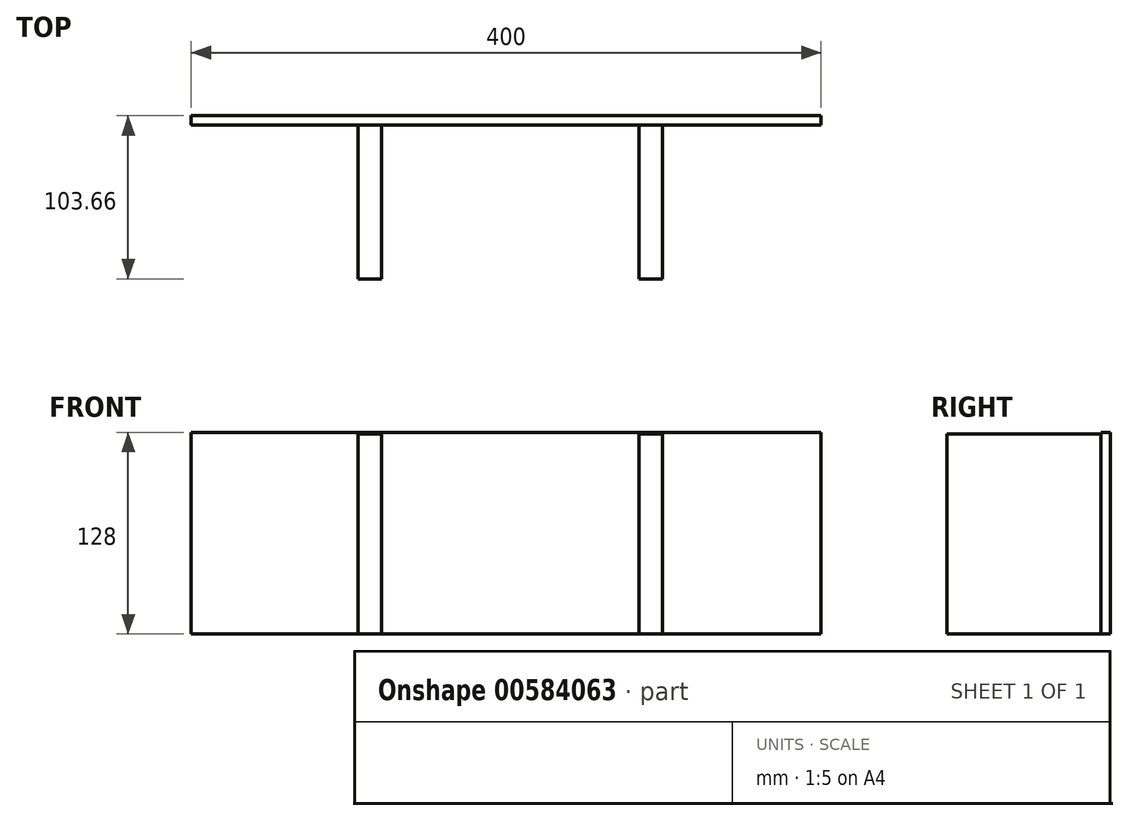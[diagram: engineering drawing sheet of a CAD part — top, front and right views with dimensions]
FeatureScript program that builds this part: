
annotation { "Feature Type Name" : "Feature", "Feature Type Description" : "" }
export const myFeature = defineFeature(function(context is Context, id is Id, definition is map)
    precondition{}
    {
        {
            var Q0;
            Q0=qCreatedBy(makeId("Top.planeOp"),FACE);
            var sketch = newSketch(context, id + "F0", { "sketchPlane" : qUnion([Q0])});
            skLineSegment(sketch, "E0", {"start": v(0, 0) * mm, "end": v(-400, 0) * mm});
            skLineSegment(sketch, "E1", {"start": v(-400, 0) * mm, "end": v(-400, 6) * mm});
            skLineSegment(sketch, "E2", {"start": v(-400, 6) * mm, "end": v(0, 6) * mm});
            skLineSegment(sketch, "E3", {"start": v(-288.1, 0) * mm, "end": v(-288.1, 135.12) * mm});
            skLineSegment(sketch, "E4", {"start": v(-107.92, 135.12) * mm, "end": v(-107.92, 0) * mm});
            skFitSpline(sketch, "E5", {"points": [v(-288.1, 135.12) * mm, v(-400, 6) * mm], "startDerivative": vector(-80.86, -186.65) * mm, "endDerivative": vector(-112.78, -106.22) * mm});
            skFitSpline(sketch, "E6", {"points": [v(-288.1, 135.12) * mm, v(-227.53, 52.45) * mm, v(-188.43, 41.47) * mm, v(-107.92, 135.12) * mm], "startDerivative": vector(134.06, -172.38) * mm, "endDerivative": vector(416.65, 700.38) * mm});
            skFitSpline(sketch, "E7", {"points": [v(-107.92, 135.12) * mm, v(-83.39, 92.79) * mm, v(0, 6) * mm], "startDerivative": vector(-18.81, 13.3) * mm, "endDerivative": vector(158.87, -141.96) * mm});
            skLineSegment(sketch, "E8", {"start": v(-376.94, 26.68) * mm, "end": v(-376.94, 6) * mm});
            skLineSegment(sketch, "E9", {"start": v(-362.4, 41.4) * mm, "end": v(-362.4, 6) * mm});
            skLineSegment(sketch, "E10", {"start": v(-348.72, 52.04) * mm, "end": v(-348.72, 6) * mm});
            skLineSegment(sketch, "E11", {"start": v(-335.96, 64.72) * mm, "end": v(-335.96, 6) * mm});
            skLineSegment(sketch, "E12", {"start": v(-322.75, 79.43) * mm, "end": v(-322.75, 6) * mm});
            skLineSegment(sketch, "E13", {"start": v(-311.95, 93.3) * mm, "end": v(-311.95, 6) * mm});
            skLineSegment(sketch, "E14", {"start": v(-299.65, 112.23) * mm, "end": v(-299.65, 6) * mm});
            skLineSegment(sketch, "E15", {"start": v(-272.67, 112.23) * mm, "end": v(-272.67, 6) * mm});
            skLineSegment(sketch, "E16", {"start": v(-260.72, 93.3) * mm, "end": v(-260.72, 6) * mm});
            skLineSegment(sketch, "E17", {"start": v(-240.1, 64.72) * mm, "end": v(-240.1, 6) * mm});
            skLineSegment(sketch, "E18", {"start": v(-251.42, 79.43) * mm, "end": v(-251.42, 6) * mm});
            skLineSegment(sketch, "E19", {"start": v(-227.53, 52.45) * mm, "end": v(-227.53, 6) * mm});
            skLineSegment(sketch, "E20", {"start": v(-216.13, 45.83) * mm, "end": v(-216.13, 6) * mm});
            skLineSegment(sketch, "E21", {"start": v(-205.23, 42.66) * mm, "end": v(-205.23, 6) * mm});
            skLineSegment(sketch, "E22", {"start": v(-188.43, 41.47) * mm, "end": v(-188.43, 6) * mm});
            skLineSegment(sketch, "E23", {"start": v(-175.91, 42.85) * mm, "end": v(-175.91, 6) * mm});
            skLineSegment(sketch, "E24", {"start": v(-164.84, 50.37) * mm, "end": v(-164.84, 6) * mm});
            skLineSegment(sketch, "E25", {"start": v(-152.72, 64.72) * mm, "end": v(-152.72, 6) * mm});
            skLineSegment(sketch, "E26", {"start": v(-142.44, 79.43) * mm, "end": v(-142.44, 6) * mm});
            skLineSegment(sketch, "E27", {"start": v(-130.69, 97.68) * mm, "end": v(-130.69, 6) * mm});
            skLineSegment(sketch, "E28", {"start": v(-120.01, 115) * mm, "end": v(-120.01, 6) * mm});
            skLineSegment(sketch, "E29", {"start": v(-97.77, 115) * mm, "end": v(-97.77, 6) * mm});
            skLineSegment(sketch, "E30", {"start": v(-83.39, 97.68) * mm, "end": v(-83.39, 6) * mm});
            skLineSegment(sketch, "E31", {"start": v(-73.37, 79.43) * mm, "end": v(-73.37, 6) * mm});
            skLineSegment(sketch, "E32", {"start": v(-60.95, 64.72) * mm, "end": v(-60.95, 6) * mm});
            skLineSegment(sketch, "E33", {"start": v(-47.5, 50.37) * mm, "end": v(-47.5, 6) * mm});
            skLineSegment(sketch, "E34", {"start": v(-32.34, 34.9) * mm, "end": v(-32.34, 6) * mm});
            skLineSegment(sketch, "E35", {"start": v(-21.72, 25.6) * mm, "end": v(-21.72, 6) * mm});
            skLineSegment(sketch, "E36", {"start": v(-288.1, 135.12) * mm, "end": v(-288.1, -8.35) * mm});
            skLineSegment(sketch, "E37", {"start": v(-294.13, 122.34) * mm, "end": v(-294.13, -97.66) * mm});
            skLineSegment(sketch, "E38", {"start": v(-279.13, 122.34) * mm, "end": v(-279.13, -97.66) * mm});
            skLineSegment(sketch, "E39", {"start": v(-294.13, -97.66) * mm, "end": v(-279.13, -97.66) * mm});
            skLineSegment(sketch, "E40", {"start": v(-115.57, 122.34) * mm, "end": v(-115.57, -97.66) * mm});
            skLineSegment(sketch, "E41", {"start": v(-115.57, -97.66) * mm, "end": v(-100.57, -97.66) * mm});
            skLineSegment(sketch, "E42", {"start": v(-100.57, -97.66) * mm, "end": v(-100.57, 122.34) * mm});
            skLineSegment(sketch, "E43", {"start": v(0, 6) * mm, "end": v(0, 0) * mm});
            skSolve(sketch);
        }
        {
            var Q0;
            Q0=sQuery(id+"F0.wireOp",EDGE,"E8");
            var Q1;
            Q1=sQuery(id+"F0.wireOp",EDGE,"E9");
            var Q2;
            Q2=sQuery(id+"F0.wireOp",EDGE,"E10");
            var Q3;
            Q3=sQuery(id+"F0.wireOp",EDGE,"E11");
            var Q4;
            Q4=sQuery(id+"F0.wireOp",EDGE,"E12");
            var Q5;
            Q5=sQuery(id+"F0.wireOp",EDGE,"E13");
            var Q6;
            Q6=sQuery(id+"F0.wireOp",EDGE,"E14");
            var Q7;
            Q7=sQuery(id+"F0.wireOp",EDGE,"E37");
            var Q8;
            Q8=sQuery(id+"F0.wireOp",EDGE,"E38");
            var Q9;
            Q9=sQuery(id+"F0.wireOp",EDGE,"E15");
            var Q10;
            Q10=sQuery(id+"F0.wireOp",EDGE,"E3");
            var Q11;
            Q11=sQuery(id+"F0.wireOp",EDGE,"E16");
            var Q12;
            Q12=sQuery(id+"F0.wireOp",EDGE,"E18");
            var Q13;
            Q13=sQuery(id+"F0.wireOp",EDGE,"E17");
            var Q14;
            Q14=sQuery(id+"F0.wireOp",EDGE,"E19");
            var Q15;
            Q15=sQuery(id+"F0.wireOp",EDGE,"E20");
            var Q16;
            Q16=sQuery(id+"F0.wireOp",EDGE,"E21");
            var Q17;
            Q17=sQuery(id+"F0.wireOp",EDGE,"E22");
            var Q18;
            Q18=sQuery(id+"F0.wireOp",EDGE,"E23");
            var Q19;
            Q19=sQuery(id+"F0.wireOp",EDGE,"E24");
            var Q20;
            Q20=sQuery(id+"F0.wireOp",EDGE,"E25");
            var Q21;
            Q21=sQuery(id+"F0.wireOp",EDGE,"E26");
            var Q22;
            Q22=sQuery(id+"F0.wireOp",EDGE,"E27");
            var Q23;
            Q23=sQuery(id+"F0.wireOp",EDGE,"E28");
            var Q24;
            Q24=sQuery(id+"F0.wireOp",EDGE,"E40");
            var Q25;
            Q25=sQuery(id+"F0.wireOp",EDGE,"E4");
            var Q26;
            Q26=sQuery(id+"F0.wireOp",EDGE,"E42");
            var Q27;
            Q27=sQuery(id+"F0.wireOp",EDGE,"E29");
            var Q28;
            Q28=sQuery(id+"F0.wireOp",EDGE,"E30");
            var Q29;
            Q29=sQuery(id+"F0.wireOp",EDGE,"E31");
            var Q30;
            Q30=sQuery(id+"F0.wireOp",EDGE,"E32");
            var Q31;
            Q31=sQuery(id+"F0.wireOp",EDGE,"E33");
            var Q32;
            Q32=sQuery(id+"F0.wireOp",EDGE,"E34");
            var Q33;
            Q33=sQuery(id+"F0.wireOp",EDGE,"E35");
            extrude(context, id + "F1", {"bodyType" : ToolBodyType.SURFACE, "surfaceEntities" : qUnion([Q0, Q1, Q2, Q3, Q4, Q5, Q6, Q7, Q8, Q9, Q10, Q11, Q12, Q13, Q14, Q15, Q16, Q17, Q18, Q19, Q20, Q21, Q22, Q23, Q24, Q25, Q26, Q27, Q28, Q29, Q30, Q31, Q32, Q33]), "depth" : 130 * mm, "offsetDistance" : 25 * mm});
        }
        {
            var Q0;
            {var subQ9=sQuery(id+"F0.wireOp",EDGE,"E1");Q0=makeQuery(id+"F0.imprint","IMPRINT",FACE,{"disambiguationData":[TD([[makeQuery(id+"F0.imprint","IMPRINT",EDGE,{"derivedFrom":subQ9}),-1.0]])]});}
            var Q1;
            {var subQ0=sQuery(id+"F0.wireOp",EDGE,"E38");var subQ1=sQuery(id+"F0.wireOp",EDGE,"E0");var subQ2=makeQuery(id+"F0.imprint","INTERSECT",VERTEX,{"derivedFrom":[subQ1,subQ0]});Q1=makeQuery(id+"F0.imprint","IMPRINT",FACE,{"disambiguationData":[TD([[makeQuery(id+"F0.imprint","IMPRINT",EDGE,{"disambiguationData":[TD([[subQ2,-1.0]])],"derivedFrom":subQ1}),-1.0]])]});}
            var Q2;
            {var subQ0=sQuery(id+"F0.wireOp",EDGE,"E36");var subQ1=sQuery(id+"F0.wireOp",EDGE,"E0");var subQ2=makeQuery(id+"F0.imprint","INTERSECT",VERTEX,{"derivedFrom":[subQ1,subQ0]});Q2=makeQuery(id+"F0.imprint","IMPRINT",FACE,{"disambiguationData":[TD([[makeQuery(id+"F0.imprint","IMPRINT",EDGE,{"disambiguationData":[TD([[subQ2,-1.0]])],"derivedFrom":subQ1}),-1.0]])]});}
            var Q3;
            {var subQ3=sQuery(id+"F0.wireOp",EDGE,"E40");var subQ4=sQuery(id+"F0.wireOp",EDGE,"E0");var subQ5=makeQuery(id+"F0.imprint","INTERSECT",VERTEX,{"derivedFrom":[subQ4,subQ3]});Q3=makeQuery(id+"F0.imprint","IMPRINT",FACE,{"disambiguationData":[TD([[makeQuery(id+"F0.imprint","IMPRINT",EDGE,{"disambiguationData":[TD([[subQ5,-1.0]])],"derivedFrom":subQ4}),-1.0]])]});}
            var Q4;
            {var subQ0=sQuery(id+"F0.wireOp",EDGE,"E4");var subQ1=sQuery(id+"F0.wireOp",EDGE,"E0");var subQ2=makeQuery(id+"F0.imprint","INTERSECT",VERTEX,{"derivedFrom":[subQ1,subQ0]});Q4=makeQuery(id+"F0.imprint","IMPRINT",FACE,{"disambiguationData":[TD([[makeQuery(id+"F0.imprint","IMPRINT",EDGE,{"disambiguationData":[TD([[subQ2,-1.0]])],"derivedFrom":subQ1}),-1.0]])]});}
            var Q5;
            {var subQ0=sQuery(id+"F0.wireOp",EDGE,"E4");var subQ1=sQuery(id+"F0.wireOp",EDGE,"E0");var subQ2=makeQuery(id+"F0.imprint","INTERSECT",VERTEX,{"derivedFrom":[subQ1,subQ0]});Q5=makeQuery(id+"F0.imprint","IMPRINT",FACE,{"disambiguationData":[TD([[makeQuery(id+"F0.imprint","IMPRINT",EDGE,{"disambiguationData":[TD([[subQ2,1.0]])],"derivedFrom":subQ1}),-1.0]])]});}
            var Q6;
            {var subQ0=sQuery(id+"F0.wireOp",EDGE,"E43");Q6=makeQuery(id+"F0.imprint","IMPRINT",FACE,{"disambiguationData":[TD([[makeQuery(id+"F0.imprint","IMPRINT",EDGE,{"derivedFrom":subQ0}),-1.0]])]});}
            extrude(context, id + "F2", {"entities" : qUnion([Q0, Q1, Q2, Q3, Q4, Q5, Q6]), "depth" : 128 * mm, "offsetDistance" : 25 * mm});
        }
        {
            var Q0;
            Q0=sQuery(id+"F0.wireOp",EDGE,"E5");
            var Q1;
            Q1=sQuery(id+"F0.wireOp",EDGE,"E6");
            var Q2;
            Q2=makeQuery(id+"F1.opExtrude","SWEPT_FACE",FACE,{"disambiguationData":[OSD([sQuery(id+"F0.wireOp",EDGE,"E11")])]});
            extrude(context, id + "F3", {"bodyType" : ToolBodyType.SURFACE, "surfaceEntities" : qUnion([Q0, Q1]), "depth" : 130 * mm, "endBoundEntityFace" : qUnion([Q2]), "offsetDistance" : 25 * mm});
        }
        {
            var Q0;
            {var subQ0=sQuery(id+"F0.wireOp",EDGE,"E39");Q0=makeQuery(id+"F0.imprint","IMPRINT",FACE,{"disambiguationData":[TD([[makeQuery(id+"F0.imprint","IMPRINT",EDGE,{"derivedFrom":subQ0}),1.0]])]});}
            var Q1;
            {var subQ0=sQuery(id+"F0.wireOp",EDGE,"E41");Q1=makeQuery(id+"F0.imprint","IMPRINT",FACE,{"disambiguationData":[TD([[makeQuery(id+"F0.imprint","IMPRINT",EDGE,{"derivedFrom":subQ0}),1.0]])]});}
            extrude(context, id + "F4", {"entities" : qUnion([Q0, Q1]), "operationType" : NewBodyOperationType.ADD, "depth" : 127 * mm, "offsetDistance" : 25 * mm});
        }
        {
            var Q0;
            Q0=sQuery(id+"F0.wireOp",EDGE,"E7");
            extrude(context, id + "F5", {"bodyType" : ToolBodyType.SURFACE, "surfaceEntities" : qUnion([Q0]), "depth" : 132 * mm, "offsetDistance" : 25 * mm});
        }
    });
